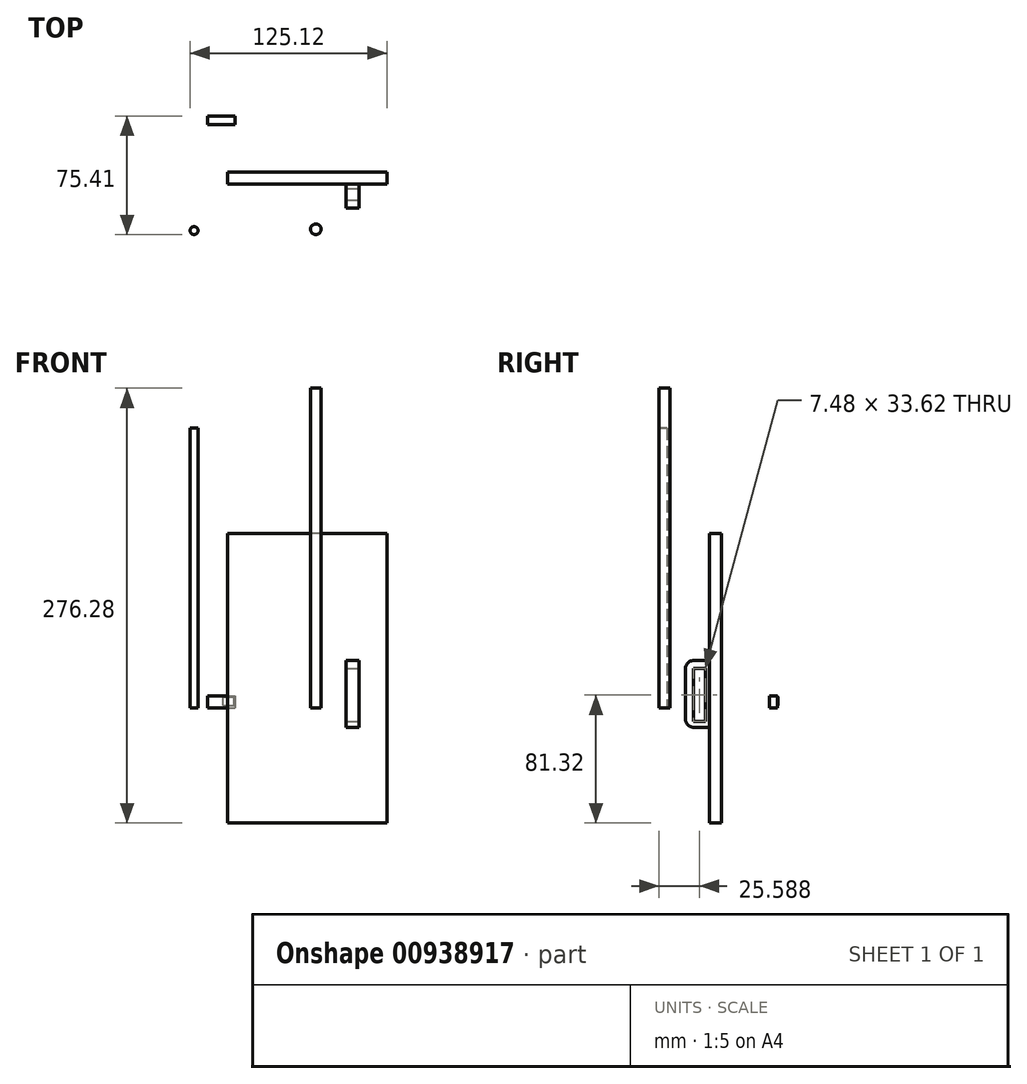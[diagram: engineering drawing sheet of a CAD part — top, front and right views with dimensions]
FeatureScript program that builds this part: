
annotation { "Feature Type Name" : "Feature", "Feature Type Description" : "" }
export const myFeature = defineFeature(function(context is Context, id is Id, definition is map)
    precondition{}
    {
        {
            var Q0;
            Q0=qCreatedBy(makeId("Top.planeOp"),FACE);
            var sketch = newSketch(context, id + "F0", { "sketchPlane" : qUnion([Q0])});
            skLineSegment(sketch, "E0.bottom", {"start": v(-43.94, 30.32) * mm, "end": v(-31.55, 30.32) * mm});
            skLineSegment(sketch, "E0.top", {"start": v(-43.94, 35.53) * mm, "end": v(-31.55, 35.53) * mm});
            skLineSegment(sketch, "E0.left", {"start": v(-43.94, 30.32) * mm, "end": v(-43.94, 35.53) * mm});
            skLineSegment(sketch, "E0.right", {"start": v(-31.55, 30.32) * mm, "end": v(-31.55, 35.53) * mm});
            skSolve(sketch);
        }
        {
            var Q0;
            Q0=makeQuery(id+"F0.imprint","IMPRINT",FACE,{"disambiguationData":[TD([[makeQuery(id+"F0.imprint","IMPRINT",EDGE,{"derivedFrom":sQuery(id+"F0.wireOp",EDGE,"E0.bottom")}),1.0]])]});
            extrude(context, id + "F1", {"entities" : qUnion([Q0]), "depth" : 7.62 * mm, "offsetDistance" : 25.4 * mm});
        }
        {
            var Q0;
            Q0=makeQuery(id+"F1.opExtrude","SWEPT_FACE",FACE,{"disambiguationData":[OSD([sQuery(id+"F0.wireOp",EDGE,"E0.right")])]});
            extrude(context, id + "F2", {"entities" : qUnion([Q0]), "operationType" : NewBodyOperationType.ADD, "depth" : 5.08 * mm, "offsetDistance" : 25.4 * mm});
        }
        {
            var Q0;
            {var subQ0=sQuery(id+"F0.wireOp",EDGE,"E0.top");Q0=makeQuery(id+"F2.boolean.opBoolean","MERGE",FACE,{"derivedFrom":[makeQuery(id+"F1.opExtrude","SWEPT_FACE",FACE,{"disambiguationData":[OSD([subQ0])]}),makeQuery(id+"F2.opExtrude","SWEPT_FACE",FACE,{"disambiguationData":[OSD([subQ0,sQuery(id+"F0.wireOp",EDGE,"E0.right")])]})]});}
            var sketch = newSketch(context, id + "F3", { "sketchPlane" : qUnion([Q0])});
            skLineSegment(sketch, "E1.bottom", {"start": v(34.07, 1.6) * mm, "end": v(27.26, 1.6) * mm});
            skLineSegment(sketch, "E1.top", {"start": v(34.07, 6.88) * mm, "end": v(27.26, 6.88) * mm});
            skLineSegment(sketch, "E1.left", {"start": v(34.07, 1.6) * mm, "end": v(34.07, 6.88) * mm});
            skLineSegment(sketch, "E1.right", {"start": v(27.26, 1.6) * mm, "end": v(27.26, 6.88) * mm});
            skSolve(sketch);
        }
        {
            var Q0;
            Q0=makeQuery(id+"F3.imprint","IMPRINT",FACE,{"disambiguationData":[TD([[makeQuery(id+"F3.imprint","IMPRINT",EDGE,{"derivedFrom":sQuery(id+"F3.wireOp",EDGE,"E1.bottom")}),-1.0]])]});
            extrude(context, id + "F4", {"entities" : qUnion([Q0]), "operationType" : NewBodyOperationType.ADD, "depth" : 0.25 * mm, "offsetDistance" : 25.4 * mm});
        }
        {
            var Q0;
            Q0=qCreatedBy(makeId("Top.planeOp"),FACE);
            var sketch = newSketch(context, id + "F5", { "sketchPlane" : qUnion([Q0])});
            skCircle(sketch, "E2", {"center": v(-52.67, -37.1) * mm, "radius": 2.54 * mm});
            skSolve(sketch);
        }
        {
            var Q0;
            Q0=makeQuery(id+"F5.imprint","IMPRINT",FACE,{"disambiguationData":[TD([[makeQuery(id+"F5.imprint","IMPRINT",EDGE,{"derivedFrom":sQuery(id+"F5.wireOp",EDGE,"E2")}),1.0]])]});
            extrude(context, id + "F6", {"entities" : qUnion([Q0]), "depth" : 177.8 * mm, "offsetDistance" : 25.4 * mm});
        }
        {
            var Q0;
            Q0=qCreatedBy(makeId("Top.planeOp"),FACE);
            var sketch = newSketch(context, id + "F7", { "sketchPlane" : qUnion([Q0])});
            skCircle(sketch, "E3", {"center": v(24.71, -36.24) * mm, "radius": 3.37 * mm});
            skSolve(sketch);
        }
        {
            var Q0;
            Q0=makeQuery(id+"F7.imprint","IMPRINT",FACE,{"disambiguationData":[TD([[makeQuery(id+"F7.imprint","IMPRINT",EDGE,{"derivedFrom":sQuery(id+"F7.wireOp",EDGE,"E3")}),1.0]])]});
            extrude(context, id + "F8", {"entities" : qUnion([Q0]), "depth" : 203.2 * mm, "offsetDistance" : 25.4 * mm});
        }
        {
            var Q0;
            Q0=qCreatedBy(makeId("Front.planeOp"),FACE);
            var sketch = newSketch(context, id + "F9", { "sketchPlane" : qUnion([Q0])});
            skLineSegment(sketch, "E4.bottom", {"start": v(69.9, 110.95) * mm, "end": v(-31.36, 110.95) * mm});
            skLineSegment(sketch, "E4.top", {"start": v(69.9, -73.08) * mm, "end": v(-31.36, -73.08) * mm});
            skLineSegment(sketch, "E4.left", {"start": v(69.9, 110.95) * mm, "end": v(69.9, -73.08) * mm});
            skLineSegment(sketch, "E4.right", {"start": v(-31.36, 110.95) * mm, "end": v(-31.36, -73.08) * mm});
            skSolve(sketch);
        }
        {
            var Q0;
            Q0=makeQuery(id+"F9.imprint","IMPRINT",FACE,{"disambiguationData":[TD([[makeQuery(id+"F9.imprint","IMPRINT",EDGE,{"derivedFrom":sQuery(id+"F9.wireOp",EDGE,"E4.bottom")}),1.0]])]});
            extrude(context, id + "F10", {"entities" : qUnion([Q0]), "depth" : 7.62 * mm, "offsetDistance" : 25.4 * mm});
        }
        {
            var Q0;
            Q0=makeQuery(id+"F10.opExtrude","CAP_FACE",FACE,{"disambiguationData":[OSD([sQuery(id+"F9.wireOp",EDGE,"E4.bottom"),sQuery(id+"F9.wireOp",EDGE,"E4.top"),sQuery(id+"F9.wireOp",EDGE,"E4.left"),sQuery(id+"F9.wireOp",EDGE,"E4.right")])],"isStart":false});
            var sketch = newSketch(context, id + "F11", { "sketchPlane" : qUnion([Q0])});
            skLineSegment(sketch, "E5.bottom", {"start": v(43.88, 30.13) * mm, "end": v(52.2, 30.13) * mm});
            skLineSegment(sketch, "E5.top", {"start": v(43.88, -12.26) * mm, "end": v(52.2, -12.26) * mm});
            skLineSegment(sketch, "E5.left", {"start": v(43.88, 30.13) * mm, "end": v(43.88, -12.26) * mm});
            skLineSegment(sketch, "E5.right", {"start": v(52.2, 30.13) * mm, "end": v(52.2, -12.26) * mm});
            skSolve(sketch);
        }
        {
            var Q0;
            Q0=makeQuery(id+"F11.imprint","IMPRINT",FACE,{"disambiguationData":[TD([[makeQuery(id+"F11.imprint","IMPRINT",EDGE,{"derivedFrom":sQuery(id+"F11.wireOp",EDGE,"E5.bottom")}),-1.0]])]});
            extrude(context, id + "F12", {"entities" : qUnion([Q0]), "operationType" : NewBodyOperationType.ADD, "depth" : 15.24 * mm, "offsetDistance" : 25.4 * mm});
        }
        {
            var Q0;
            Q0=makeQuery(id+"F12.opExtrude","CAP_EDGE",EDGE,{"disambiguationData":[OSD([sQuery(id+"F11.wireOp",EDGE,"E5.bottom")])],"isStart":false});
            var Q1;
            Q1=makeQuery(id+"F12.opExtrude","CAP_EDGE",EDGE,{"disambiguationData":[OSD([sQuery(id+"F11.wireOp",EDGE,"E5.top")])],"isStart":false});
            fillet(context, id + "F13", {"entities" : qUnion([Q0, Q1]), "radius" : 5.08 * mm, "tangentPropagation" : true, "allowEdgeOverflow" : false});
        }
        {
            var Q0;
            Q0=makeQuery(id+"F12.opExtrude","SWEPT_FACE",FACE,{"disambiguationData":[OSD([sQuery(id+"F11.wireOp",EDGE,"E5.right")])]});
            var sketch = newSketch(context, id + "F14", { "sketchPlane" : qUnion([Q0])});
            skLineSegment(sketch, "E6.bottom", {"start": v(-17.78, 25.05) * mm, "end": v(-10.3, 25.05) * mm});
            skLineSegment(sketch, "E6.top", {"start": v(-17.78, -8.57) * mm, "end": v(-10.3, -8.57) * mm});
            skLineSegment(sketch, "E6.left", {"start": v(-17.78, 25.05) * mm, "end": v(-17.78, -8.57) * mm});
            skLineSegment(sketch, "E6.right", {"start": v(-10.3, 25.05) * mm, "end": v(-10.3, -8.57) * mm});
            skSolve(sketch);
        }
        {
            var Q0;
            Q0=makeQuery(id+"F14.imprint","IMPRINT",FACE,{"disambiguationData":[TD([[makeQuery(id+"F14.imprint","IMPRINT",EDGE,{"derivedFrom":sQuery(id+"F14.wireOp",EDGE,"E6.bottom")}),-1.0]])]});
            extrude(context, id + "F15", {"entities" : qUnion([Q0]), "operationType" : NewBodyOperationType.REMOVE, "oppositeDirection" : true, "depth" : 10.16 * mm, "offsetDistance" : 25.4 * mm});
        }
    });
